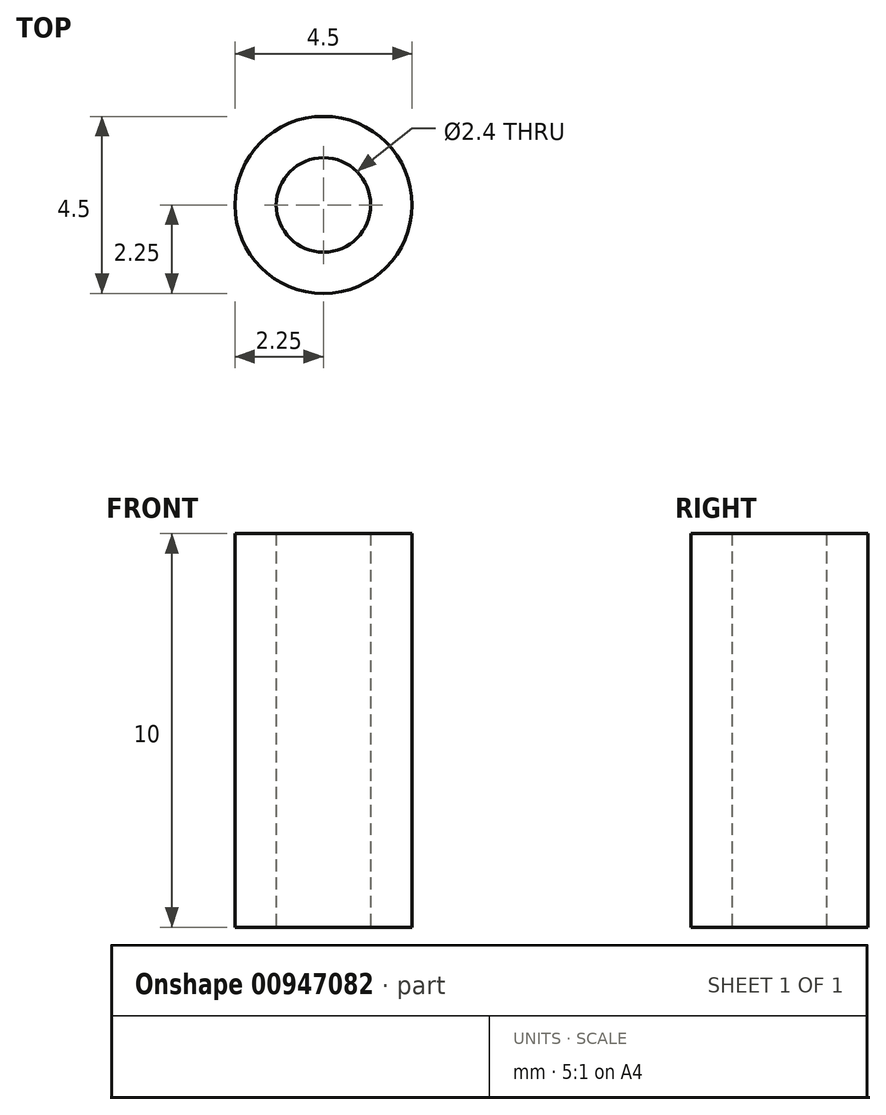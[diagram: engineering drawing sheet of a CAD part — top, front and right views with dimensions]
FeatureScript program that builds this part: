
annotation { "Feature Type Name" : "Feature", "Feature Type Description" : "" }
export const myFeature = defineFeature(function(context is Context, id is Id, definition is map)
    precondition{}
    {
        {
            var Q0;
            Q0=qCreatedBy(makeId("Top.planeOp"),FACE);
            var sketch = newSketch(context, id + "F0", { "sketchPlane" : qUnion([Q0])});
            skCircle(sketch, "E0", {"center": v(0, 0) * mm, "radius": 2.25 * mm});
            skCircle(sketch, "E1", {"center": v(0, 0) * mm, "radius": 1.2 * mm});
            skPoint(sketch, "E2", {"position": v(0, 2.25) * mm});
            skPoint(sketch, "E3", {"position": v(0, 1.2) * mm});
            skPoint(sketch, "E4", {"position": v(0, -2.25) * mm});
            skSolve(sketch);
        }
        {
            var Q0;
            Q0=makeQuery(id+"F0.imprint","IMPRINT",FACE,{"disambiguationData":[TD([[makeQuery(id+"F0.imprint","IMPRINT",EDGE,{"derivedFrom":sQuery(id+"F0.wireOp",EDGE,"E0")}),1.0]])]});
            extrude(context, id + "F1", {"entities" : qUnion([Q0]), "depth" : 10 * mm, "offsetDistance" : 25 * mm});
        }
    });
